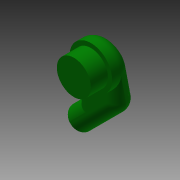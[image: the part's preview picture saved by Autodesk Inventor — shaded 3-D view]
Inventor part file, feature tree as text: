
AUTODESK INVENTOR PART (.ipt)
format: ipt  version: 2015 (Build 190159000, 159)  size: 394,752 bytes
history: native  units: mm
features: sketch x10, extrude x9, fillet x4, plane x1, split x1
ambient origin geometry x8: Origin, YZ Plane, XZ Plane, XY Plane, X Axis, Y Axis, Z Axis, Center Point
bodies: Solid1 (feature_tree), Solid4 (feature_tree), Solid5 (feature_tree)
feature tree (25):
  extrude  "Extrusion1"  Depth=2.0mm TaperAngle=0.0deg
  extrude  "Extrusion2"  Depth=4.75mm
  extrude  "Extrusion3"  Depth=1.4mm
  fillet  "Fillet1"  Radius=3.25mm
  extrude  "Extrusion4"  Depth=3.25mm TaperAngle=0.0deg
  extrude  "Extrusion5"  Depth=10.0mm TaperAngle=0.0deg
  fillet  "Fillet2"  Radius=1.3mm
  extrude  "Extrusion8"  Depth=1.3mm
  fillet  "Fillet4"  Radius=3.8mm
  extrude  "Extrusion10"  Depth=0.25mm
  plane  "Work Plane2"
  extrude  "Extrusion11"  Depth=2.0mm TaperAngle=0.0deg
  fillet  "Fillet5"  Radius=2.6mm
  extrude  "Extrusion12"  [1 undecoded]
  split  "Split2"
  sketch  "Sketch1"  dims[d0=4.0mm d1=2.0mm d2=0.0mm]
  sketch  "Sketch2"  dims[d3=2.5mm d4=4.75mm]
  sketch  "Sketch3"  dims[d5=3.25mm d6=0.0mm d8=1.4mm d9=3.25mm d10=0.0mm]
  sketch  "Sketch4"  dims[d11=1.5mm d12=3.25mm d13=0.0mm]
  sketch  "Sketch6"  dims[d14=1.5mm d15=10.0mm d16=0.0mm d17=1.3mm]
  sketch  "Sketch10"  dims[d25=0.655mm d26=0.0mm d27=1.3mm d31=3.8mm d32=0.0mm]
  sketch  "Sketch13"  dims[d33=5.8mm d34=0.0mm d35=0.25mm]
  sketch  "Sketch14"  dims[d36=2.0mm d37=2.0mm d38=0.0mm d39=2.6mm]
  sketch  "Sketch15"
  sketch  "Sketch16"
note: 1 required parameter value undecoded (feature->parameter linkage not recoverable at this tier; creation-order binding heuristic only, values carry confidence <= 0.55)
